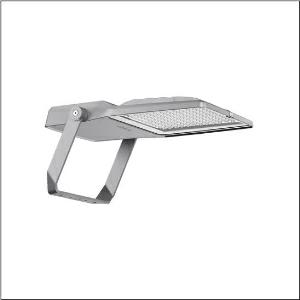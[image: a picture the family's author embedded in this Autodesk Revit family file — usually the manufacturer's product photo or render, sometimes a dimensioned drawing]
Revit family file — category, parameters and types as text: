
# Revit family: floodlight_fl_21_iq_midi___rs12_5xa7781e6b1a_09af
name_source: partatom
category: Lighting Fixtures
units: mm (PartAtom-declared; Revit-internal decimal feet)

## family parameters
Cut with Voids When Loaded = No
Host = Face
Light Source = No
Part Type = Normal
Room Calculation Point = No
Round Connector Dimension = Use Diameter
Shared = No

## types (1)
- --- (1 x LED, 21420 lm, 208.1 W, 5700K)
    Apparent Load = 208 VA
    CIE Flux Codes = 79 92 99 100 100
    Color Rendering = 90
    Color Temperature = 5700K
    Default Elevation = 1800 mm
    Description = Floodlight FL 21 iQ midi, floodlight, primary light control with lens, of PMMA, primary optical cover: protective disc, of toughened safety glass, transparent, light distribution: RS12, light emission: direct distribution, installation type: surface-mounted, LED, High Power LED, rated luminous flux: 21.420lm, luminous efficacy: 103lm/W, light colour: 957, colour temperature: 5700K, control gear: ECG iQ, control: optimised constant luminous flux control (CLO 2.0), Desk-Remote (wireless, voltage-free reading and setting of iQ features in the workshop via application-optimized NFC function/RFID function), Light-Fading, Smart-Wire, Night-Set, Lumen-Switch, Temp-Guard, Auto-Match, with terminal, 6-pole, mains connection: 220..240V, AC, 50/60Hz, start of lifetime: 208W, end of service life: 227W, reduction: 90W, luminaire housing, of diecast aluminium, powder-coated, Siteco® metallic grey (DB 702S), corrosivity category C5 mid according to DIN EN ISO 12944, sealing non-destructively replaceable, mounting bracket, of steel, galvanised, powder-coated, Siteco® metallic grey (DB 702S), protection rating (complete): IP66, insulation class (complete): insulation class II (safety insulation), certification: CE, protection symbol: D, impact resistance: IK08, permissible operating ambient temperature: -40..+40°C, permissible operating ambient temperature for outdoor applications: -40..+50°C, standard: DIN EN 12944, LABS conformity tested according to VDMA 24364:2018-05, packaging unit: 1 piece

Light Distribution: RS12
    Height = 76 mm
    Lamp = 1 x LED
    Lamp Light Flux = 21420 lm
    Lamp Power = 208.1 W
    Lamp count = 1
    Length = 657 mm
    Luminous efficacy = 103 lm/W
    Manufacturer = Siteco
    ModVariant = No
    Model = 5XA7781E6B1A
    Number of Poles = 1
    OnlyDefault = Yes
    Power Factor = 1
    Product Name = Floodlight FL 21 iQ midi | RS12
    Product group = floodlight | pylon annexe
    ProductGroupID = 6200
    Protection Class = Protection class II
    Protection Degree = IP 66
    RLX_Detail_Level = 1
    RLX_Emergency_Light_Flux = 0 lm
    RLX_Emergency_Type = 0
    RLX_Emergency_Type_DB = No
    RlxData = <blob elided: 141341 chars, md5=d761062c>
    Socket = socket
    Standby Power = 0 W
    System Light Flux = 21420 lm
    System Power = 208 W
    Type Comments = factory setting: luminous flux: 100 % | dim-lin: 254 | 710 mA
    Type Image = l_1006876.jpg
    URL = http://relux.com
    VarID = @adj_037793
    Voltage = 0 V
    Weight = 0.00 kg
    Width = 442 mm

## geometry (parser evidence)
native form markers: Blend x4, Sweep x13
no freeform markers — native parametric forms only
